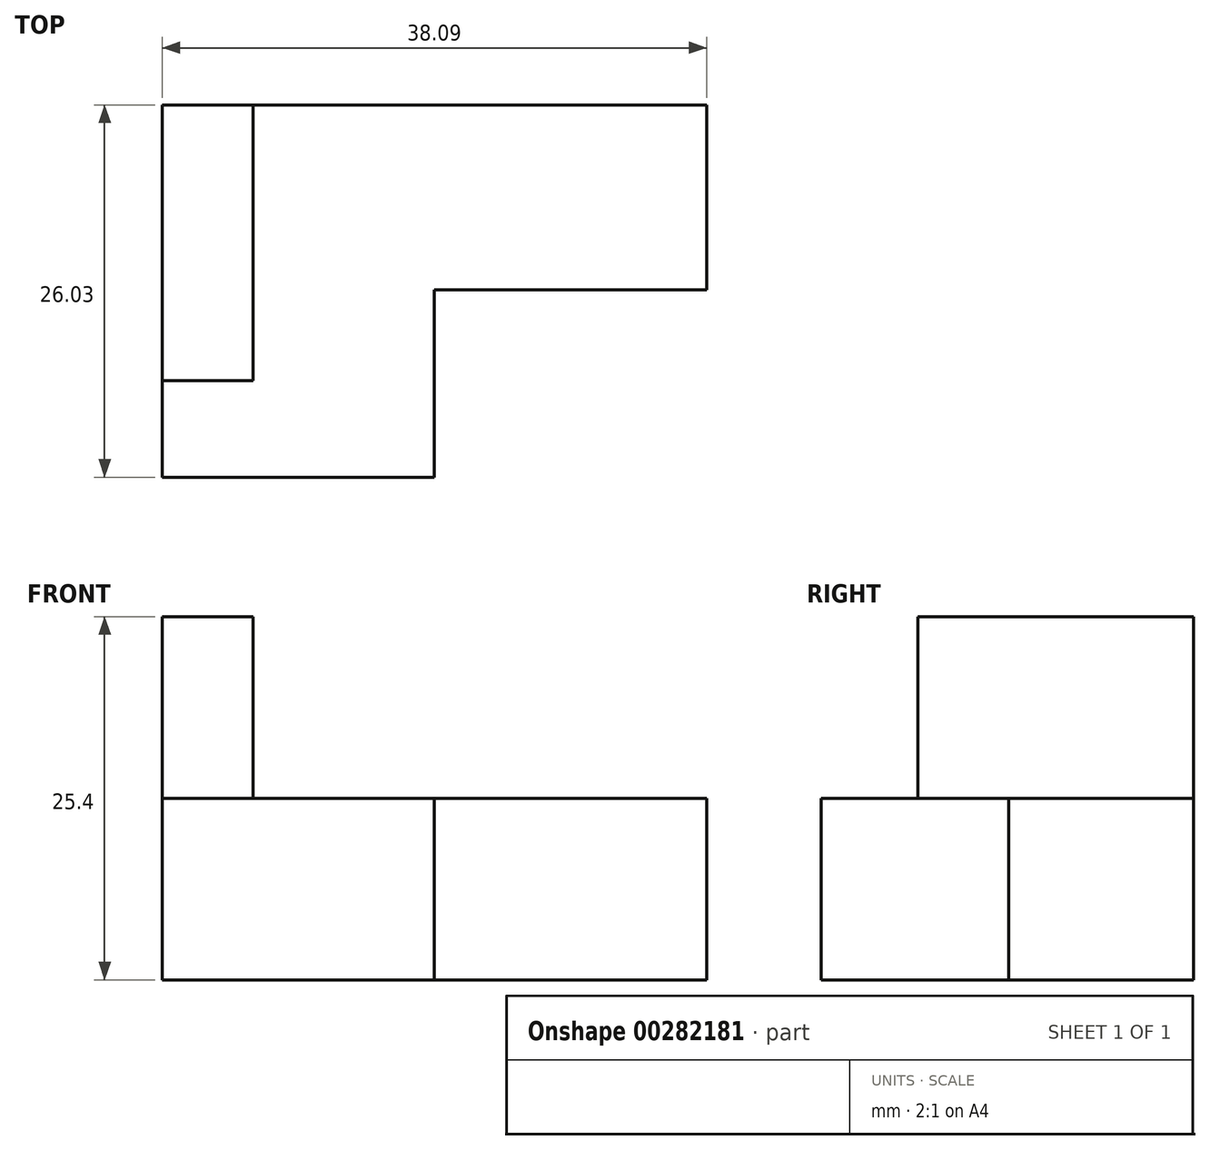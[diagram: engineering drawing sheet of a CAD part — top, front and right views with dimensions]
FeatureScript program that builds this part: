
annotation { "Feature Type Name" : "Feature", "Feature Type Description" : "" }
export const myFeature = defineFeature(function(context is Context, id is Id, definition is map)
    precondition{}
    {
        {
            var Q0;
            Q0=qCreatedBy(makeId("Top.planeOp"),FACE);
            var sketch = newSketch(context, id + "F0", { "sketchPlane" : qUnion([Q0])});
            skLineSegment(sketch, "E0", {"start": v(0, 0) * mm, "end": v(0, 26.03) * mm});
            skLineSegment(sketch, "E1", {"start": v(0, 26.03) * mm, "end": v(38.09, 26.03) * mm});
            skLineSegment(sketch, "E2", {"start": v(38.09, 26.03) * mm, "end": v(38.09, 13.1) * mm});
            skLineSegment(sketch, "E3", {"start": v(38.09, 13.1) * mm, "end": v(19.04, 13.1) * mm});
            skPoint(sketch, "E3.endSnap0", {"position": v(19.04, 26.03) * mm});
            skLineSegment(sketch, "E4", {"start": v(19.04, 13.1) * mm, "end": v(19.04, 0) * mm});
            skLineSegment(sketch, "E5", {"start": v(19.04, 0) * mm, "end": v(0, 0) * mm});
            skSolve(sketch);
        }
        {
            var Q0;
            Q0 = qSketchRegion(id + "F0", true);
            extrude(context, id + "F1", {"entities" : qUnion([Q0]), "depth" : 12.7 * mm});
        }
        {
            var Q0;
            Q0=makeQuery(id+"F1.opExtrude","CAP_FACE",FACE,{"disambiguationData":[OSD([sQuery(id+"F0.wireOp",EDGE,"E0"),sQuery(id+"F0.wireOp",EDGE,"E1"),sQuery(id+"F0.wireOp",EDGE,"E2"),sQuery(id+"F0.wireOp",EDGE,"E3"),sQuery(id+"F0.wireOp",EDGE,"E4"),sQuery(id+"F0.wireOp",EDGE,"E5")])],"isStart":false});
            var sketch = newSketch(context, id + "F2", { "sketchPlane" : qUnion([Q0])});
            skLineSegment(sketch, "E6.bottom", {"start": v(0, 26.03) * mm, "end": v(6.38, 26.03) * mm});
            skLineSegment(sketch, "E6.top", {"start": v(0, 6.76) * mm, "end": v(6.38, 6.76) * mm});
            skLineSegment(sketch, "E6.left", {"start": v(0, 26.03) * mm, "end": v(0, 6.76) * mm});
            skLineSegment(sketch, "E6.right", {"start": v(6.38, 26.03) * mm, "end": v(6.38, 6.76) * mm});
            skSolve(sketch);
        }
        {
            var Q0;
            Q0 = qSketchRegion(id + "F2", true);
            extrude(context, id + "F3", {"entities" : qUnion([Q0]), "operationType" : NewBodyOperationType.ADD, "depth" : 12.7 * mm});
        }
    });
